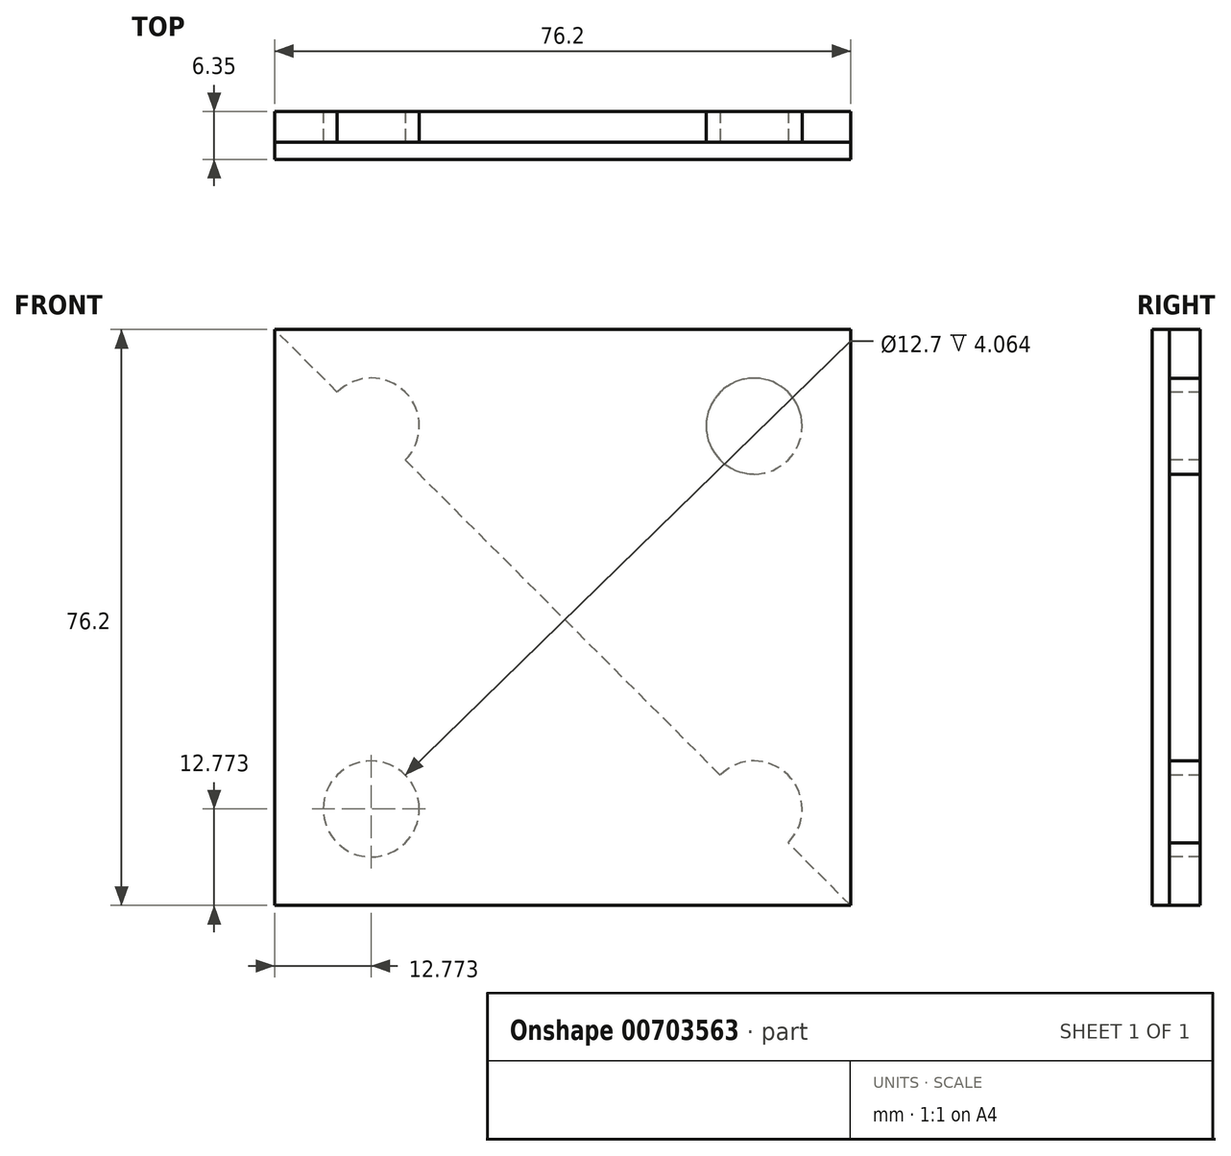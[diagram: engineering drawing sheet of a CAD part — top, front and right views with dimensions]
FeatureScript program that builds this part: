
annotation { "Feature Type Name" : "Feature", "Feature Type Description" : "" }
export const myFeature = defineFeature(function(context is Context, id is Id, definition is map)
    precondition{}
    {
        {
            var Q0;
            Q0=qCreatedBy(makeId("Front.planeOp"),FACE);
            var sketch = newSketch(context, id + "F0", { "sketchPlane" : qUnion([Q0])});
            skLineSegment(sketch, "E0.bottom", {"start": v(38.1, 38.1) * mm, "end": v(-38.1, 38.1) * mm});
            skLineSegment(sketch, "E0.top", {"start": v(38.1, -38.1) * mm, "end": v(-38.1, -38.1) * mm});
            skLineSegment(sketch, "E0.left", {"start": v(38.1, 38.1) * mm, "end": v(38.1, -38.1) * mm});
            skLineSegment(sketch, "E0.right", {"start": v(-38.1, 38.1) * mm, "end": v(-38.1, -38.1) * mm});
            skPoint(sketch, "E0.middle", {"position": v(0, 0) * mm});
            skSolve(sketch);
        }
        {
            var Q0;
            Q0=makeQuery(id+"F0.imprint","IMPRINT",FACE,{"disambiguationData":[TD([[makeQuery(id+"F0.imprint","IMPRINT",EDGE,{"derivedFrom":sQuery(id+"F0.wireOp",EDGE,"E0.bottom")}),1.0]])]});
            extrude(context, id + "F1", {"entities" : qUnion([Q0]), "depth" : 2.3 * mm, "offsetDistance" : 25.4 * mm});
        }
        {
            var Q0;
            Q0=makeQuery(id+"F1.opExtrude","CAP_FACE",FACE,{"disambiguationData":[OSD([sQuery(id+"F0.wireOp",EDGE,"E0.bottom"),sQuery(id+"F0.wireOp",EDGE,"E0.top"),sQuery(id+"F0.wireOp",EDGE,"E0.left"),sQuery(id+"F0.wireOp",EDGE,"E0.right")])],"isStart":true});
            var sketch = newSketch(context, id + "F2", { "sketchPlane" : qUnion([Q0])});
            skLineSegment(sketch, "E1", {"start": v(38.1, -38.1) * mm, "end": v(-38.1, 38.1) * mm});
            skLineSegment(sketch, "E2", {"start": v(-38.1, -38.1) * mm, "end": v(38.1, 38.1) * mm});
            skCircle(sketch, "E3", {"center": v(25.33, -25.33) * mm, "radius": 6.35 * mm});
            skCircle(sketch, "E4.1.0", {"center": v(-25.33, -25.33) * mm, "radius": 6.35 * mm});
            skCircle(sketch, "E4.2.0", {"center": v(-25.33, 25.33) * mm, "radius": 6.35 * mm});
            skCircle(sketch, "E4.3.0", {"center": v(25.33, 25.33) * mm, "radius": 6.35 * mm});
            skPoint(sketch, "E4.center", {"position": v(0, 0) * mm});
            skLineSegment(sketch, "E4.anchor1", {"start": v(0, 0) * mm, "end": v(25.33, -25.33) * mm, "construction": true});
            skLineSegment(sketch, "E4.anchor2", {"start": v(0, 0) * mm, "end": v(25.33, 25.33) * mm, "construction": true});
            skSolve(sketch);
        }
        {
            var Q0;
            {var subQ0=sQuery(id+"F2.wireOp",EDGE,"E3");var subQ1=sQuery(id+"F2.wireOp",EDGE,"E1");var subQ2=makeQuery(id+"F2.imprint","INTERSECT",VERTEX,{"disambiguationData":[OD(0.0)],"derivedFrom":[subQ1,subQ0]});Q0=makeQuery(id+"F2.imprint","IMPRINT",FACE,{"disambiguationData":[TD([[makeQuery(id+"F2.imprint","IMPRINT",EDGE,{"disambiguationData":[TD([[subQ2,-1.0]])],"derivedFrom":subQ1}),1.0]])]});}
            var Q1;
            {var subQ0=sQuery(id+"F2.wireOp",EDGE,"E4.1.0");var subQ1=sQuery(id+"F2.wireOp",EDGE,"E2");var subQ2=makeQuery(id+"F2.imprint","INTERSECT",VERTEX,{"disambiguationData":[OD(0.0)],"derivedFrom":[subQ1,subQ0]});Q1=makeQuery(id+"F2.imprint","IMPRINT",FACE,{"disambiguationData":[TD([[makeQuery(id+"F2.imprint","IMPRINT",EDGE,{"disambiguationData":[TD([[subQ2,-1.0]])],"derivedFrom":subQ1}),-1.0]])]});}
            var Q2;
            {var subQ0=sQuery(id+"F2.wireOp",EDGE,"E4.1.0");var subQ1=sQuery(id+"F2.wireOp",EDGE,"E2");var subQ2=makeQuery(id+"F2.imprint","INTERSECT",VERTEX,{"disambiguationData":[OD(0.0)],"derivedFrom":[subQ1,subQ0]});Q2=makeQuery(id+"F2.imprint","IMPRINT",FACE,{"disambiguationData":[TD([[makeQuery(id+"F2.imprint","IMPRINT",EDGE,{"disambiguationData":[TD([[subQ2,-1.0]])],"derivedFrom":subQ1}),1.0]])]});}
            var Q3;
            {var subQ0=sQuery(id+"F2.wireOp",EDGE,"E4.2.0");var subQ1=sQuery(id+"F2.wireOp",EDGE,"E1");var subQ2=makeQuery(id+"F2.imprint","INTERSECT",VERTEX,{"disambiguationData":[OD(0.0)],"derivedFrom":[subQ1,subQ0]});Q3=makeQuery(id+"F2.imprint","IMPRINT",FACE,{"disambiguationData":[TD([[makeQuery(id+"F2.imprint","IMPRINT",EDGE,{"disambiguationData":[TD([[subQ2,-1.0]])],"derivedFrom":subQ1}),1.0]])]});}
            var Q4;
            {var subQ0=sQuery(id+"F2.wireOp",EDGE,"E4.2.0");var subQ1=sQuery(id+"F2.wireOp",EDGE,"E1");var subQ2=makeQuery(id+"F2.imprint","INTERSECT",VERTEX,{"disambiguationData":[OD(0.0)],"derivedFrom":[subQ1,subQ0]});Q4=makeQuery(id+"F2.imprint","IMPRINT",FACE,{"disambiguationData":[TD([[makeQuery(id+"F2.imprint","IMPRINT",EDGE,{"disambiguationData":[TD([[subQ2,-1.0]])],"derivedFrom":subQ1}),-1.0]])]});}
            var Q5;
            {var subQ0=sQuery(id+"F2.wireOp",EDGE,"E4.3.0");var subQ1=sQuery(id+"F2.wireOp",EDGE,"E2");var subQ2=makeQuery(id+"F2.imprint","INTERSECT",VERTEX,{"disambiguationData":[OD(0.0)],"derivedFrom":[subQ1,subQ0]});Q5=makeQuery(id+"F2.imprint","IMPRINT",FACE,{"disambiguationData":[TD([[makeQuery(id+"F2.imprint","IMPRINT",EDGE,{"disambiguationData":[TD([[subQ2,-1.0]])],"derivedFrom":subQ1}),1.0]])]});}
            var Q6;
            {var subQ0=sQuery(id+"F2.wireOp",EDGE,"E4.3.0");var subQ1=sQuery(id+"F2.wireOp",EDGE,"E2");var subQ2=makeQuery(id+"F2.imprint","INTERSECT",VERTEX,{"disambiguationData":[OD(0.0)],"derivedFrom":[subQ1,subQ0]});Q6=makeQuery(id+"F2.imprint","IMPRINT",FACE,{"disambiguationData":[TD([[makeQuery(id+"F2.imprint","IMPRINT",EDGE,{"disambiguationData":[TD([[subQ2,-1.0]])],"derivedFrom":subQ1}),-1.0]])]});}
            var Q7;
            {var subQ0=sQuery(id+"F2.wireOp",EDGE,"E3");var subQ1=sQuery(id+"F2.wireOp",EDGE,"E1");var subQ2=makeQuery(id+"F2.imprint","INTERSECT",VERTEX,{"disambiguationData":[OD(0.0)],"derivedFrom":[subQ1,subQ0]});Q7=makeQuery(id+"F2.imprint","IMPRINT",FACE,{"disambiguationData":[TD([[makeQuery(id+"F2.imprint","IMPRINT",EDGE,{"disambiguationData":[TD([[subQ2,-1.0]])],"derivedFrom":subQ1}),-1.0]])]});}
            extrude(context, id + "F3", {"entities" : qUnion([Q0, Q1, Q2, Q3, Q4, Q5, Q6, Q7]), "operationType" : NewBodyOperationType.ADD, "depth" : 4.06 * mm, "offsetDistance" : 25.4 * mm});
        }
    });
